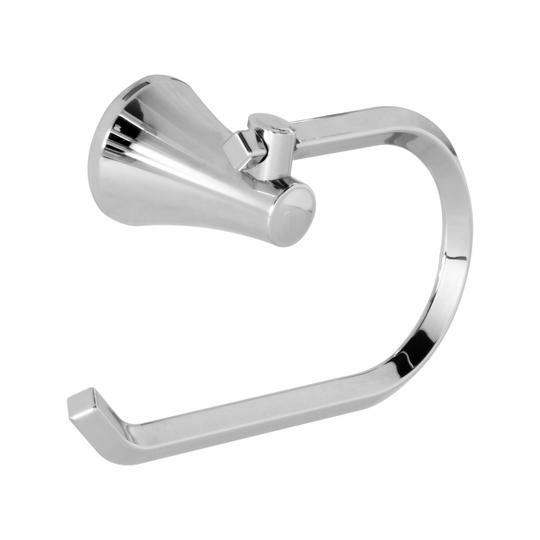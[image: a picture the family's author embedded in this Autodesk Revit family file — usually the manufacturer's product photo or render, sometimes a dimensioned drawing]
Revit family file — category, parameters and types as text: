
# Revit family: BL-2503-11 PORTARROLLO CONTEMPRA
name_source: partatom
category: Plumbing Fixtures
revit_build: Autodesk Revit 2018 (Build: 20170223_1515(x64)
units: mm (PartAtom-declared; Revit-internal decimal feet)

## family parameters
Cut with Voids When Loaded = No
Host = Face
OmniClass Number = 23.31.11.00
Part Type = Normal
Room Calculation Point = No
Round Connector Dimension = Use Diameter
Shared = No

## types (1)
- BL-2503-11
    Alto gancho = 105 mm
    Alto soporte = 70 mm  [stored 0.229659 ft]
    Ancho gancho = 181 mm  [stored 0.593832 ft]
    CW Connection = Yes
    Default Elevation = 0 mm  [stored 0 ft]
    Description = Portarrollo
    Diametro base = 50 mm  [stored 0.164042 ft]
    HW Connection = Yes
    Link Ficha Tecnica = http://infotecnica.gricol.com
    Manufacturer = Gricol
    Model = BL-2503-11
    Plastico ABS cromado = Plastico - ABS Cromado
    Product Name = PORTARROLLO CONTEMPRA
    Type Image = PORTARROLLO CONTEMPRA.jpg
    URL = https://www.gricol.com
    Vent Connection = No
    Waste Connection = No

note: [stored X ft] marks values corroborated as IEEE doubles in the binary element streams (Revit-internal decimal feet)

## geometry (parser evidence)
native form markers: Blend x2, Sweep x5
no freeform markers — native parametric forms only
